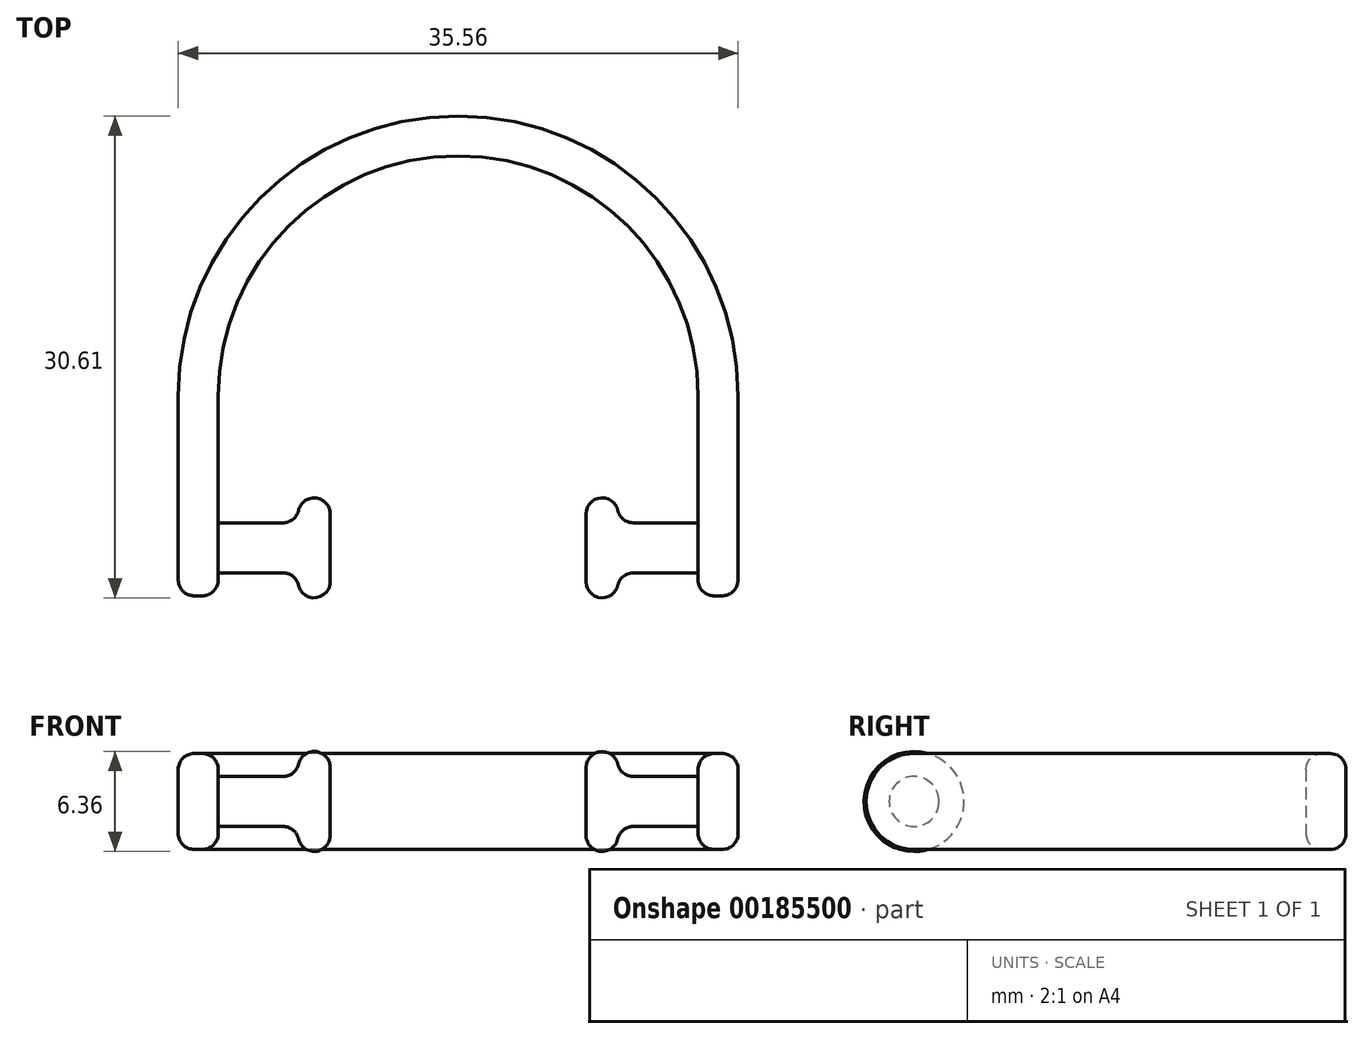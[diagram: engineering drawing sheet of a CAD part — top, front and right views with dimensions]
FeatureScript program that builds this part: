
annotation { "Feature Type Name" : "Feature", "Feature Type Description" : "" }
export const myFeature = defineFeature(function(context is Context, id is Id, definition is map)
    precondition{}
    {
        {
            var Q0;
            Q0=qCreatedBy(makeId("Top.planeOp"),FACE);
            var sketch = newSketch(context, id + "F0", { "sketchPlane" : qUnion([Q0])});
            skArc(sketch, "E0", {"start": v(-15.24, 9.65) * mm, "mid": v(0, 24.9) * mm, "end": v(15.24, 9.65) * mm});
            skLineSegment(sketch, "E1", {"start": v(-15.24, 9.65) * mm, "end": v(-15.24, -3.05) * mm});
            skLineSegment(sketch, "E2", {"start": v(-17.78, -3.05) * mm, "end": v(-17.78, 9.65) * mm});
            skLineSegment(sketch, "E3", {"start": v(0, 67.15) * mm, "end": v(0, -19.72) * mm, "construction": true});
            skLineSegment(sketch, "E4", {"start": v(-17.78, -3.05) * mm, "end": v(-15.24, -3.05) * mm});
            skLineSegment(sketch, "E5.MirrorCS", {"start": v(17.78, -3.05) * mm, "end": v(15.24, -3.05) * mm});
            skLineSegment(sketch, "E6.MirrorCS", {"start": v(15.24, 9.65) * mm, "end": v(15.24, -3.05) * mm});
            skLineSegment(sketch, "E7.MirrorCS", {"start": v(17.78, -3.05) * mm, "end": v(17.78, 9.65) * mm});
            skArc(sketch, "E8", {"start": v(-17.78, 9.65) * mm, "mid": v(0, 27.43) * mm, "end": v(17.78, 9.65) * mm});
            skSolve(sketch);
        }
        {
            var Q0;
            Q0 = qSketchRegion(id + "F0", true);
            extrude(context, id + "F1", {"entities" : qUnion([Q0]), "endBound" : BoundingType.SYMMETRIC, "depth" : 6.1 * mm});
        }
        {
            var Q0;
            Q0=qCreatedBy(makeId("Top.planeOp"),FACE);
            var sketch = newSketch(context, id + "F2", { "sketchPlane" : qUnion([Q0])});
            skLineSegment(sketch, "E9", {"start": v(-15.24, 0) * mm, "end": v(-8.13, 0) * mm});
            skLineSegment(sketch, "E10", {"start": v(-8.13, 0) * mm, "end": v(-8.13, 3.18) * mm});
            skLineSegment(sketch, "E11", {"start": v(-8.13, 3.18) * mm, "end": v(-10.16, 3.18) * mm});
            skLineSegment(sketch, "E12", {"start": v(-10.16, 3.18) * mm, "end": v(-10.16, 1.59) * mm});
            skLineSegment(sketch, "E13", {"start": v(-10.16, 1.59) * mm, "end": v(-15.24, 1.59) * mm});
            skLineSegment(sketch, "E14", {"start": v(-15.24, 1.59) * mm, "end": v(-15.24, 0) * mm});
            skLineSegment(sketch, "E15", {"start": v(0, 27.07) * mm, "end": v(0, -22.76) * mm, "construction": true});
            skLineSegment(sketch, "E16.MirrorCS", {"start": v(15.24, 0) * mm, "end": v(8.13, 0) * mm});
            skLineSegment(sketch, "E17.MirrorCS", {"start": v(15.24, 1.59) * mm, "end": v(15.24, 0) * mm});
            skLineSegment(sketch, "E18.MirrorCS", {"start": v(10.16, 1.59) * mm, "end": v(15.24, 1.59) * mm});
            skLineSegment(sketch, "E19.MirrorCS", {"start": v(10.16, 3.18) * mm, "end": v(10.16, 1.59) * mm});
            skLineSegment(sketch, "E20.MirrorCS", {"start": v(43.07, 0) * mm, "end": v(-47.77, 0) * mm, "construction": true});
            skLineSegment(sketch, "E21.MirrorCS", {"start": v(8.13, 3.17) * mm, "end": v(10.16, 3.17) * mm});
            skLineSegment(sketch, "E22.MirrorCS", {"start": v(8.13, 0) * mm, "end": v(8.13, 3.18) * mm});
            skSolve(sketch);
        }
        {
            var Q0;
            Q0 = qSketchRegion(id + "F2", true);
            var Q1;
            Q1=sQuery(id+"F2.wireOp",EDGE,"E20.MirrorCS");
            revolve(context, id + "F3", {"operationType" : NewBodyOperationType.ADD, "entities" : qUnion([Q0]), "axis" : qUnion([Q1]), "revolveType" : RevolveType.FULL});
        }
        {
            var Q0;
            Q0=makeQuery(id+"F1.opExtrude","CAP_EDGE",EDGE,{"disambiguationData":[OSD([sQuery(id+"F0.wireOp",EDGE,"E4")])],"isStart":true});
            var Q1;
            Q1=makeQuery(id+"F1.opExtrude","CAP_EDGE",EDGE,{"disambiguationData":[OSD([sQuery(id+"F0.wireOp",EDGE,"E4")])],"isStart":false});
            var Q2;
            Q2=makeQuery(id+"F1.opExtrude","CAP_EDGE",EDGE,{"disambiguationData":[OSD([sQuery(id+"F0.wireOp",EDGE,"E5.MirrorCS")])],"isStart":false});
            var Q3;
            Q3=makeQuery(id+"F1.opExtrude","CAP_EDGE",EDGE,{"disambiguationData":[OSD([sQuery(id+"F0.wireOp",EDGE,"E5.MirrorCS")])],"isStart":true});
            fillet(context, id + "F4", {"entities" : qUnion([Q0, Q1, Q2, Q3]), "radius" : 3.05 * mm, "allowEdgeOverflow" : false});
        }
        {
            var Q0;
            Q0=makeQuery(id+"F1.opExtrude","CAP_EDGE",EDGE,{"disambiguationData":[OSD([sQuery(id+"F0.wireOp",EDGE,"E8")])],"isStart":false});
            fillet(context, id + "F5", {"entities" : qUnion([Q0]), "radius" : 1.02 * mm, "tangentPropagation" : true, "allowEdgeOverflow" : false});
        }
        {
            var Q0;
            Q0=makeQuery(id+"F1.opExtrude","CAP_EDGE",EDGE,{"disambiguationData":[OSD([sQuery(id+"F0.wireOp",EDGE,"E0")])],"isStart":false});
            fillet(context, id + "F6", {"entities" : qUnion([Q0]), "radius" : 1.02 * mm, "tangentPropagation" : true, "allowEdgeOverflow" : false});
        }
        {
            var Q0;
            Q0=makeQuery(id+"F3.opRevolve","SWEPT_EDGE",EDGE,{"disambiguationData":[OSD([sQuery(id+"F2.wireOp",EDGE,"E10"),sQuery(id+"F2.wireOp",EDGE,"E11")])]});
            var Q1;
            Q1=makeQuery(id+"F3.opRevolve","SWEPT_EDGE",EDGE,{"disambiguationData":[OSD([sQuery(id+"F2.wireOp",EDGE,"E21.MirrorCS"),sQuery(id+"F2.wireOp",EDGE,"E22.MirrorCS")])]});
            var Q2;
            Q2=makeQuery(id+"F3.opRevolve","SWEPT_EDGE",EDGE,{"disambiguationData":[OSD([sQuery(id+"F2.wireOp",EDGE,"E11"),sQuery(id+"F2.wireOp",EDGE,"E12")])]});
            var Q3;
            Q3=makeQuery(id+"F3.opRevolve","SWEPT_EDGE",EDGE,{"disambiguationData":[OSD([sQuery(id+"F2.wireOp",EDGE,"E19.MirrorCS"),sQuery(id+"F2.wireOp",EDGE,"E21.MirrorCS")])]});
            fillet(context, id + "F7", {"entities" : qUnion([Q0, Q1, Q2, Q3]), "radius" : 1.02 * mm, "tangentPropagation" : true, "allowEdgeOverflow" : false});
        }
        {
            var Q0;
            Q0=makeQuery(id+"F3.opRevolve","SWEPT_EDGE",EDGE,{"disambiguationData":[OSD([sQuery(id+"F2.wireOp",EDGE,"E17.MirrorCS"),sQuery(id+"F2.wireOp",EDGE,"E18.MirrorCS")])]});
            var Q1;
            Q1=makeQuery(id+"F3.opRevolve","SWEPT_EDGE",EDGE,{"disambiguationData":[OSD([sQuery(id+"F2.wireOp",EDGE,"E12"),sQuery(id+"F2.wireOp",EDGE,"E13")])]});
            var Q2;
            Q2=makeQuery(id+"F3.opRevolve","SWEPT_EDGE",EDGE,{"disambiguationData":[OSD([sQuery(id+"F2.wireOp",EDGE,"E13"),sQuery(id+"F2.wireOp",EDGE,"E14")])]});
            var Q3;
            Q3=makeQuery(id+"F3.opRevolve","SWEPT_EDGE",EDGE,{"disambiguationData":[OSD([sQuery(id+"F2.wireOp",EDGE,"E18.MirrorCS"),sQuery(id+"F2.wireOp",EDGE,"E19.MirrorCS")])]});
            fillet(context, id + "F8", {"entities" : qUnion([Q0, Q1, Q2, Q3]), "radius" : 1.02 * mm, "tangentPropagation" : true, "allowEdgeOverflow" : false});
        }
    });
